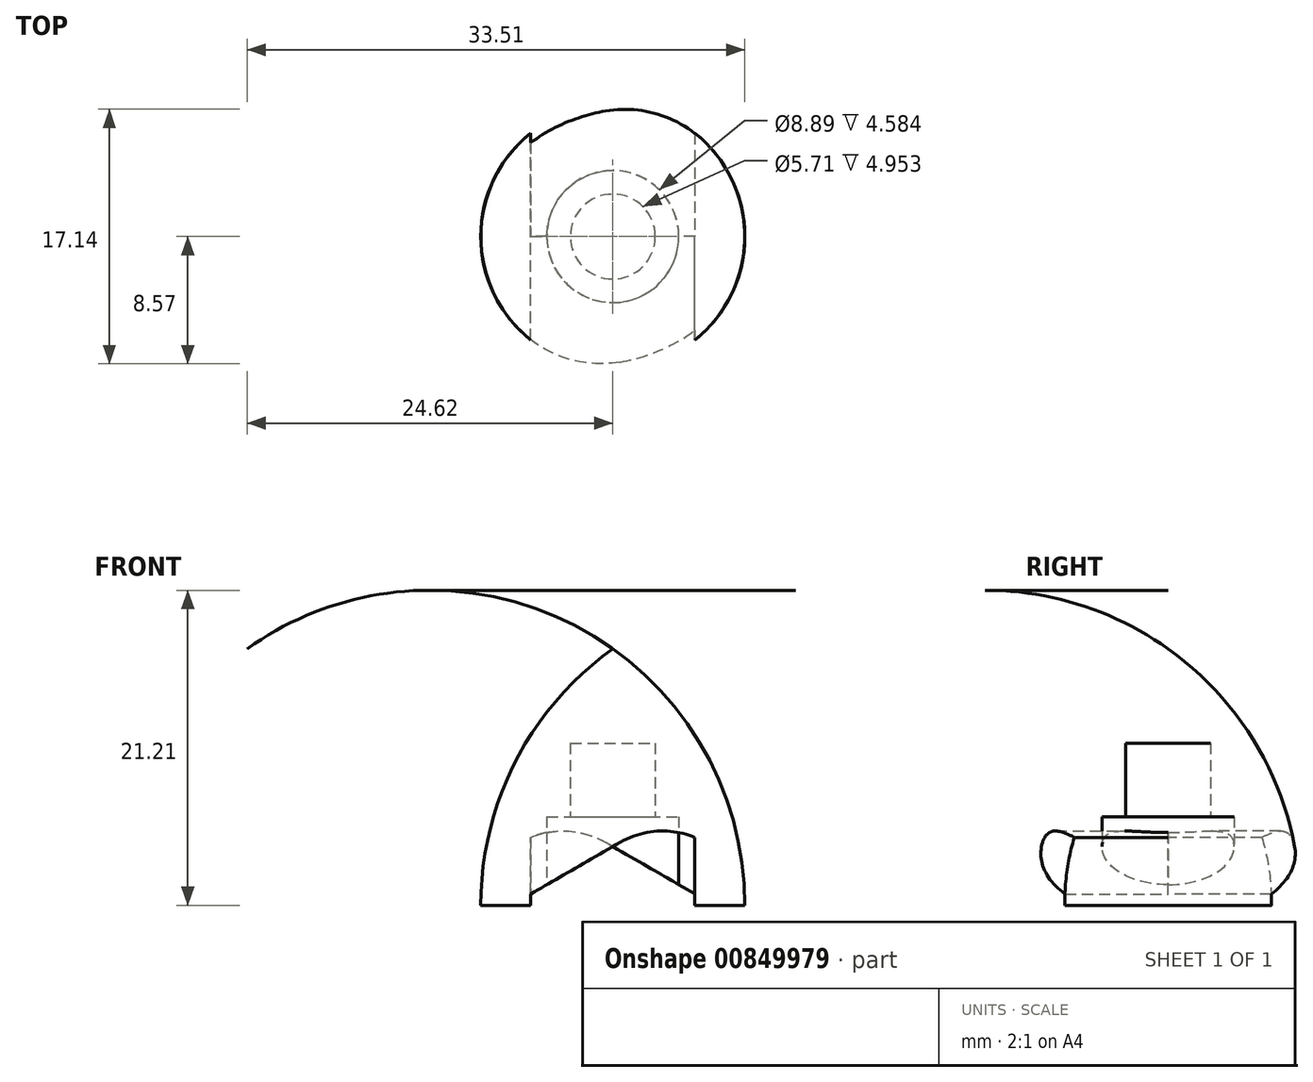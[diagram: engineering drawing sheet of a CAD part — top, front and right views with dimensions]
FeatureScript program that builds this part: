
annotation { "Feature Type Name" : "Feature", "Feature Type Description" : "" }
export const myFeature = defineFeature(function(context is Context, id is Id, definition is map)
    precondition{}
    {
        {
            var Q0;
            Q0=qCreatedBy(makeId("Front.planeOp"),FACE);
            var sketch = newSketch(context, id + "F0", { "sketchPlane" : qUnion([Q0])});
            skLineSegment(sketch, "E0", {"start": v(0, 0) * mm, "end": v(0, 26.1) * mm, "construction": true});
            skArc(sketch, "E1", {"start": v(8.9, 0) * mm, "mid": v(6.54, 9.71) * mm, "end": v(0, 17.27) * mm});
            skLineSegment(sketch, "E2", {"start": v(8.89, 0) * mm, "end": v(4.45, 0) * mm});
            skLineSegment(sketch, "E3", {"start": v(4.45, 0) * mm, "end": v(4.45, 5.97) * mm});
            skLineSegment(sketch, "E4", {"start": v(4.45, 5.97) * mm, "end": v(2.86, 5.97) * mm});
            skLineSegment(sketch, "E5", {"start": v(2.86, 5.97) * mm, "end": v(2.86, 10.92) * mm});
            skLineSegment(sketch, "E6", {"start": v(2.86, 10.92) * mm, "end": v(0, 10.92) * mm});
            skLineSegment(sketch, "E7", {"start": v(0, 17.27) * mm, "end": v(0, 10.92) * mm});
            skSolve(sketch);
        }
        {
            var Q0;
            Q0=makeQuery(id+"F0.imprint","IMPRINT",FACE,{"disambiguationData":[TD([[makeQuery(id+"F0.imprint","IMPRINT",EDGE,{"derivedFrom":sQuery(id+"F0.wireOp",EDGE,"E1")}),1.0]])]});
            var Q1;
            Q1=sQuery(id+"F0.wireOp",EDGE,"E0");
            revolve(context, id + "F1", {"surfaceOperationType" : NewSurfaceOperationType.NEW, "entities" : qUnion([Q0]), "axis" : qUnion([Q1]), "revolveType" : RevolveType.FULL});
        }
        {
            var Q0;
            Q0=qCreatedBy(makeId("Front.planeOp"),FACE);
            var sketch = newSketch(context, id + "F2", { "sketchPlane" : qUnion([Q0])});
            skLineSegment(sketch, "E8", {"start": v(-5.52, 0) * mm, "end": v(-5.52, 0.76) * mm});
            skLineSegment(sketch, "E9", {"start": v(5.52, 0) * mm, "end": v(5.52, 4.57) * mm});
            skLineSegment(sketch, "E10", {"start": v(-5.52, 0) * mm, "end": v(5.52, 0) * mm});
            skArc(sketch, "E11", {"start": v(5.52, 4.57) * mm, "mid": v(2.97, 4.99) * mm, "end": v(0.5, 4.24) * mm});
            skLineSegment(sketch, "E12", {"start": v(-5.52, 0.76) * mm, "end": v(0.5, 4.24) * mm});
            skLineSegment(sketch, "E13", {"start": v(0, 0) * mm, "end": v(0, 6.11) * mm, "construction": true});
            skSolve(sketch);
        }
        {
            var Q0;
            Q0=qCreatedBy(makeId("Front.planeOp"),FACE);
            var sketch = newSketch(context, id + "F3", { "sketchPlane" : qUnion([Q0])});
            skLineSegment(sketch, "E14", {"start": v(0, 0) * mm, "end": v(0, 6.11) * mm, "construction": true});
            skLineSegment(sketch, "E15.MirrorCS", {"start": v(5.53, 0) * mm, "end": v(5.53, 0.77) * mm});
            skLineSegment(sketch, "E16.MirrorCS", {"start": v(5.53, 0.77) * mm, "end": v(-0.49, 4.24) * mm});
            skLineSegment(sketch, "E17.MirrorCS", {"start": v(-5.52, 0) * mm, "end": v(-5.52, 4.58) * mm});
            skArc(sketch, "E18.MirrorCS", {"start": v(-5.52, 4.58) * mm, "mid": v(-2.97, 5) * mm, "end": v(-0.49, 4.24) * mm});
            skLineSegment(sketch, "E19", {"start": v(5.53, 0) * mm, "end": v(-5.52, 0) * mm});
            skSolve(sketch);
        }
        {
            var Q0;
            Q0 = qSketchRegion(id + "F2", true);
            extrude(context, id + "F4", {"entities" : qUnion([Q0]), "operationType" : NewBodyOperationType.REMOVE, "depth" : 25.4 * mm, "offsetDistance" : 25.4 * mm});
        }
        {
            var Q0;
            Q0 = qSketchRegion(id + "F3", true);
            extrude(context, id + "F5", {"entities" : qUnion([Q0]), "operationType" : NewBodyOperationType.REMOVE, "oppositeDirection" : true, "depth" : 25.4 * mm, "offsetDistance" : 25.4 * mm});
        }
    });
